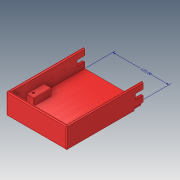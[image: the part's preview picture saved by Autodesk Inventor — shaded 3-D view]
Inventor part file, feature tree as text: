
AUTODESK INVENTOR PART (.ipt)
format: ipt  version: 2019 (Build 230136000, 136)  size: 271,872 bytes
history: native  units: mm
features: extrude x9, sketch x8, plane x3, projected_geometry x3, other x2, fillet x2
ambient origin geometry x8: Origin, YZ Plane, XZ Plane, XY Plane, X Axis, Y Axis, Z Axis, Center Point
bodies: Solid1 (feature_tree)
feature tree (27):
  other  "Annotations"
  extrude  "Extrusion1"  Depth=150.0mm
  extrude  "Extrusion2"  Depth=5.0mm
  extrude  "Extrusion3"  Depth=38.7mm TaperAngle=0.0deg
  sketch  "Sketch6"  dims[d9=3.0mm d10=20.0mm d11=0.0mm]
  fillet  "Fillet1"  Radius=3.0mm
  plane  "Work Plane4"
  extrude  "Extrusion8"  Depth=20.0mm TaperAngle=0.0deg
  extrude  "Extrusion9"  Depth=2.5mm TaperAngle=0.0deg
  fillet  "Fillet4"  Radius=35.0mm
  extrude  "Extrusion10"  Depth=16.0mm
  plane  "Work Plane5"
  extrude  "Extrusion11"  TaperAngle=0.0deg  [1 undecoded]
  plane  "Work Plane3"
  extrude  "Extrusion13"  Depth=40.0mm
  extrude  "Extrusion14"  Depth=16.0mm
  sketch  "Sketch1"  dims[d0=135.0mm d1=150.0mm]
  sketch  "Sketch3"  dims[d2=8.0mm d3=0.0mm d4=5.0mm]
  projected_geometry  "Projected Loop2"
  sketch  "Sketch4"  dims[d5=5.0mm d6=38.7mm d7=0.0mm d8=3.0mm]
  projected_geometry  "Projected Loop3"
  sketch  "Sketch15"  dims[d25=2.0mm d37=2.5mm d38=0.0mm d39=35.0mm]
  projected_geometry  "Projected Loop7"
  sketch  "Sketch16"  dims[d40=0.0mm d41=16.0mm]
  sketch  "Sketch17"  dims[d42=40.0mm d43=0.0mm]
  sketch  "Sketch21"  dims[d44=0.0mm d45=40.0mm d46=16.0mm d47=16.0mm d48=0.0mm d49=1.0mm d50=4.5mm d51=6.0mm d52=9.0mm d53=4.5mm d54=7.0mm d56=12.0mm d57=0.0mm d60=4.5mm d61=4.5mm d62=30.8mm d65=0.0mm d66=0.0mm d67=90.0mm d76=-1.5mm d78=7.5mm d79=7.5mm d80=3.15mm d81=0.0mm d90=12.5mm d91=18.0mm d92=13.0mm d93=17.0mm d94=12.0mm d95=10.0mm d96=0.0mm d73=4.870635mm d74=1.41766mm d75=125.0mm]
  other  "Linear Dimension 1"
note: 1 required parameter value undecoded (feature->parameter linkage not recoverable at this tier; creation-order binding heuristic only, values carry confidence <= 0.55)
